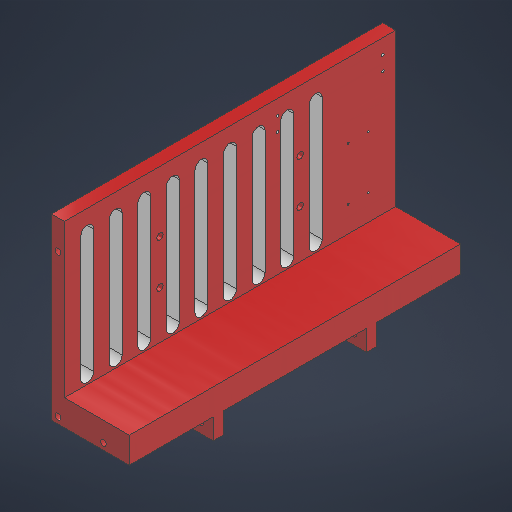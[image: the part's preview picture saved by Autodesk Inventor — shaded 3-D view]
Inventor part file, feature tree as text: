
AUTODESK INVENTOR PART (.ipt)
format: ipt  version: 2025.1 (Build 291241000, 241)  size: 940,544 bytes
history: native  units: in
note: dims shown in document units (in); Inventor stores cm internally (conversion verified against a paired STEP export)
features: sketch x20, extrude x20, projected_geometry x7, mirror x3, plane x2, fillet x1, other x1
ambient origin geometry x8: Origin, YZ Plane, XZ Plane, XY Plane, X Axis, Y Axis, Z Axis, Center Point
bodies: Solid1 (feature_tree)
feature tree (54):
  sketch  "Sketch1"  dims[d0=5.9055in d1=10.0394in]
  extrude  "Extrusion1"  Depth=10.0394in
  extrude  "Extrusion2"  Depth=0.3937in
  extrude  "Extrusion3"  Depth=0.315in
  sketch  "Sketch3"  dims[d7=0.315in d8=0.1969in d9=0.0in]
  sketch  "Sketch4"  dims[d10=5.8071in d11=0.0in d12=2.126in]
  extrude  "Extrusion4"  Depth=0.1969in TaperAngle=0.0deg
  sketch  "Sketch5"  dims[d13=0.6693in d14=0.1969in]
  extrude  "Extrusion5"  Depth=2.126in
  plane  "Work Plane1"
  mirror  "Mirror1"
  extrude  "Extrusion6"  Depth=0.1969in
  extrude  "Extrusion7"  Depth=0.1969in
  extrude  "Extrusion8"  Depth=0.1969in TaperAngle=0.0deg
  extrude  "Extrusion9"  Depth=0.3937in
  extrude  "Extrusion10"  Depth=0.3937in
  extrude  "Extrusion11"  Depth=3.937in
  fillet  "Fillet1"  Radius=3.2283in
  extrude  "Extrusion12"  Depth=2.3622in
  mirror  "Mirror2"
  extrude  "Extrusion13"  Depth=0.3937in
  extrude  "Extrusion14"  Depth=2.9528in
  extrude  "Extrusion15"  Depth=1.752in
  extrude  "Extrusion16"  Depth=0.1181in
  mirror  "Mirror3"
  extrude  "Extrusion17"  Depth=0.3937in TaperAngle=0.0deg
  sketch  "Sketch17"  dims[d37=0.1181in d38=0.3937in d39=0.0in]
  extrude  "Extrusion18"  Depth=0.7874in
  extrude  "Extrusion19"  Depth=0.3937in TaperAngle=0.0deg
  extrude  "Extrusion20"  Depth=0.3937in
  sketch  "Sketch2"  dims[d5=0.3937in d6=0.315in]
  projected_geometry  "Projected Loop1"
  plane  "Work Plane2"
  sketch  "Sketch6"  dims[d15=0.1969in d16=0.1969in]
  sketch  "Sketch7"  dims[d17=0.1969in d18=5.8071in d19=0.0in]
  projected_geometry  "Projected Loop2"
  sketch  "Sketch8"  dims[d20=0.3937in d21=0.3937in]
  projected_geometry  "Projected Loop3"
  sketch  "Sketch9"  dims[d22=0.3937in d23=0.3937in]
  sketch  "Sketch10"  dims[d24=6.2992in d25=3.937in d26=3.2283in]
  projected_geometry  "Projected Loop4"
  sketch  "Sketch11"  dims[d27=2.3622in d28=2.5197in]
  projected_geometry  "Projected Loop5"
  sketch  "Sketch13"  dims[d29=3.6614in d30=0.3937in]
  sketch  "Sketch14"  dims[d31=2.9528in d32=2.9528in]
  sketch  "Sketch15"  dims[d33=1.752in d34=0.1181in]
  projected_geometry  "Projected Loop7"
  sketch  "Sketch16"  dims[d35=0.1181in d36=0.1181in]
  projected_geometry  "Projected Loop8"
  sketch  "Sketch18"  dims[d40=135.0deg d41=0.7874in]
  sketch  "Sketch19"  dims[d42=1.9685in d43=0.3937in d44=0.0in]
  sketch  "Sketch20"  dims[d45=0.3937in d46=0.0in d47=0.5315in d48=2.4803in d49=5.9055in d50=0.1181in d51=0.1181in d52=0.3937in d53=0.0in d54=0.1437in d55=0.0in d56=0.7874in d57=0.7874in d58=0.7874in d59=0.7874in d60=0.0787in d61=0.0787in d62=0.0787in d63=0.0787in d64=0.3937in d65=0.0in d66=2.1654in d67=2.1654in d68=0.7874in d69=0.7874in d70=0.315in d71=0.315in d72=0.6299in d73=0.0in d74=0.2047in d75=5.6924in d76=0.0in d77=2.4537in d78=0.3937in d79=0.0in d80=17.2313in d81=0.0in d82=1.7323in d83=17.2313in d84=0.0in d85=0.3937in d86=0.0in d87=0.7874in d88=0.1969in d89=0.1772in d90=0.2362in d91=0.0in d92=0.1772in d93=1.378in d94=0.1772in d95=0.1969in d97=0.1772in d98=4.3307in d99=0.3937in d100=0.0in d101=9.6457in d102=4.3307in d103=0.6071in d104=1.6in d105=0.0591in d106=0.0591in d107=0.0591in d108=0.0591in d109=0.3937in d110=0.0in d111=3.189in d112=0.4331in d113=0.0787in d114=0.0787in d115=0.0787in d116=0.0787in d117=0.3937in d118=0.0in d119=8.6614in d120=3.7402in d121=0.3937in d122=0.3937in d123=3.5433in d125=0.8661in d126=0.3937in d128=0.3937in d130=0.3937in d131=0.0in]
  sketch  "Sketch Rectangular Pattern1"  dims[d3=0.3937in d4=3.6417in]
  other  "Finish1"
